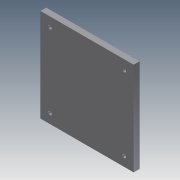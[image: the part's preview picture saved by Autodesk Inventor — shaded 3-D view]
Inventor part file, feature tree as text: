
AUTODESK INVENTOR PART (.ipt)
format: ipt  version: 2011 (Build 150239000, 239)  size: 496,640 bytes
history: native  units: in
note: dims shown in document units (in); Inventor stores cm internally (conversion verified against a paired STEP export)
features: extrude x49, sketch x49, fillet x2
ambient origin geometry x8: Origin, YZ Plane, XZ Plane, XY Plane, X Axis, Y Axis, Z Axis, Center Point
bodies: Solid1 (feature_tree)
feature tree (100):
  extrude  "Extrusion1"  Depth=4.0in
  extrude  "Extrusion2"  Depth=2.16in
  extrude  "Extrusion3"  Depth=1.7655in
  extrude  "Extrusion4"  Depth=0.029in TaperAngle=0.0deg
  extrude  "Extrusion5"  Depth=2.36in
  fillet  "Fillet1"  Radius=2.56in
  extrude  "Extrusion6"  Depth=0.125in
  extrude  "Extrusion7"  Depth=0.262in TaperAngle=0.0deg
  extrude  "Extrusion8"  Depth=0.029in TaperAngle=0.0deg
  extrude  "Extrusion9"  Depth=0.156in
  extrude  "Extrusion10"  Depth=0.5in TaperAngle=0.0deg
  extrude  "Extrusion11"  Depth=0.5in TaperAngle=0.0deg
  extrude  "Extrusion12"  Depth=1.875in TaperAngle=0.0deg
  extrude  "Extrusion13"  Depth=2.125in TaperAngle=0.0deg
  sketch  "Sketch14"  dims[d44=2.125in d45=0.0in d46=2.125in d47=0.0in]
  sketch  "Sketch15"  dims[d48=2.125in d49=0.0in d50=1.875in d51=0.0in]
  sketch  "Sketch16"  dims[d52=2.125in d53=0.0in d54=2.125in d55=0.0in]
  sketch  "Sketch17"  dims[d56=1.875in d57=0.0in d58=1.875in d59=0.0in]
  extrude  "Extrusion14"  Depth=2.125in TaperAngle=0.0deg
  extrude  "Extrusion15"  Depth=1.875in TaperAngle=0.0deg
  extrude  "Extrusion16"  Depth=2.125in TaperAngle=0.0deg
  extrude  "Extrusion17"  Depth=1.875in TaperAngle=0.0deg
  extrude  "Extrusion18"  Depth=2.125in TaperAngle=0.0deg
  extrude  "Extrusion19"  Depth=6.248in TaperAngle=0.0deg
  extrude  "Extrusion20"  Depth=1.281in
  extrude  "Extrusion21"  Depth=7.0in TaperAngle=0.0deg
  extrude  "Extrusion22"  Depth=2.0in
  extrude  "Extrusion23"  Depth=4.0in
  extrude  "Extrusion24"  Depth=2.0in
  extrude  "Extrusion25"  Depth=1.0in TaperAngle=0.0deg
  extrude  "Extrusion26"  Depth=0.25in
  extrude  "Extrusion27"  Depth=0.25in TaperAngle=0.0deg
  extrude  "Extrusion28"  Depth=0.25in TaperAngle=0.0deg
  extrude  "Extrusion29"  Depth=0.875in
  extrude  "Extrusion30"  Depth=0.5in TaperAngle=0.0deg
  extrude  "Extrusion31"  Depth=0.875in
  extrude  "Extrusion32"  Depth=0.5in TaperAngle=0.0deg
  extrude  "Extrusion33"  Depth=2.0in
  extrude  "Extrusion34"  Depth=4.0in
  fillet  "Fillet2"  Radius=1.0in
  extrude  "Extrusion35"  Depth=0.75in TaperAngle=0.0deg
  extrude  "Extrusion36"  Depth=0.9055in
  extrude  "Extrusion37"  Depth=0.8268in
  extrude  "Extrusion38"  Depth=0.75in TaperAngle=0.0deg
  extrude  "Extrusion39"  Depth=0.2559in
  extrude  "Extrusion40"  Depth=0.315in
  extrude  "Extrusion41"  Depth=1.063in
  extrude  "Extrusion42"  Depth=1.0in TaperAngle=0.0deg
  extrude  "Extrusion43"  Depth=0.406in
  extrude  "Extrusion44"  Depth=4.0in
  extrude  "Extrusion45"  [1 undecoded]
  extrude  "Extrusion46"  [1 undecoded]
  extrude  "Extrusion47"  [1 undecoded]
  extrude  "Extrusion48"  [1 undecoded]
  extrude  "Extrusion49"  [1 undecoded]
  sketch  "Sketch1"  dims[d0=4.0in d1=4.0in]
  sketch  "Sketch2"  dims[d2=0.029in d3=0.0in d4=2.16in]
  sketch  "Sketch3"  dims[d5=0.029in d6=0.0in d7=1.7655in]
  sketch  "Sketch4"  dims[d8=0.156in d9=0.029in d10=0.0in]
  sketch  "Sketch5"  dims[d11=0.029in d12=0.0in d13=2.36in d14=2.56in]
  sketch  "Sketch6"  dims[d15=0.262in d16=0.0in d17=0.125in]
  sketch  "Sketch7"  dims[d18=0.362in d19=0.0in d20=0.262in d21=0.0in]
  sketch  "Sketch8"  dims[d22=0.1in d23=0.0in d24=0.029in d25=0.0in]
  sketch  "Sketch9"  dims[d26=1.594in d27=0.156in]
  sketch  "Sketch10"  dims[d28=0.029in d29=0.0in d30=0.5in d31=0.0in]
  sketch  "Sketch11"  dims[d32=0.75in d33=0.0in d34=0.5in d35=0.0in]
  sketch  "Sketch12"  dims[d36=2.125in d37=0.0in d38=1.875in d39=0.0in]
  sketch  "Sketch13"  dims[d40=1.875in d41=0.0in d42=2.125in d43=0.0in]
  sketch  "Sketch18"  dims[d60=2.125in d61=0.0in d62=2.125in d63=0.0in]
  sketch  "Sketch19"  dims[d64=0.875in d65=0.0in d66=6.248in d67=0.0in]
  sketch  "Sketch20"  dims[d68=7.0in d69=0.0in d70=1.281in]
  sketch  "Sketch21"  dims[d71=3.188in d72=7.0in d73=0.0in]
  sketch  "Sketch22"  dims[d74=0.25in d75=0.0in d76=2.0in]
  sketch  "Sketch23"  dims[d77=2.0in d78=4.0in]
  sketch  "Sketch24"  dims[d79=1.0in d80=0.0in d81=2.0in]
  sketch  "Sketch25"  dims[d82=1.0in d83=1.0in d84=0.0in]
  sketch  "Sketch26"  dims[d85=0.5in d86=0.25in]
  sketch  "Sketch27"  dims[d87=0.25in d88=0.25in d89=0.0in]
  sketch  "Sketch28"  dims[d90=0.25in d91=0.0in d92=0.25in d93=0.0in]
  sketch  "Sketch29"  dims[d94=0.656in d95=0.875in]
  sketch  "Sketch30"  dims[d96=0.5in d97=0.0in d98=0.5in d99=0.0in]
  sketch  "Sketch31"  dims[d100=0.875in d101=0.875in]
  sketch  "Sketch32"  dims[d102=0.5in d103=0.0in d104=0.5in d105=0.0in]
  sketch  "Sketch33"  dims[d106=2.0in d107=2.0in]
  sketch  "Sketch34"  dims[d108=4.0in d109=4.0in d110=1.0in d111=0.0in]
  sketch  "Sketch35"  dims[d112=0.25in d113=0.0in d114=0.75in d115=0.0in]
  sketch  "Sketch36"  dims[d116=0.75in d117=0.0in d118=0.9055in]
  sketch  "Sketch37"  dims[d119=0.4134in d120=0.8268in]
  sketch  "Sketch38"  dims[d121=1.378in d122=0.75in d123=0.0in]
  sketch  "Sketch39"  dims[d124=0.5315in d125=0.2559in]
  sketch  "Sketch40"  dims[d126=0.315in d127=0.315in]
  sketch  "Sketch41"  dims[d128=1.063in d129=1.063in]
  sketch  "Sketch42"  dims[d130=0.0787in d131=1.0in d132=0.0in]
  sketch  "Sketch43"  dims[d133=0.25in d134=0.0in d135=0.406in]
  sketch  "Sketch44"  dims[d136=4.0in d137=4.0in]
  sketch  "Sketch45"  dims[d138=0.25in d139=0.0in]
  sketch  "Sketch46"
  sketch  "Sketch47"
  sketch  "Sketch48"
  sketch  "Sketch49"
note: 5 required parameter values undecoded (feature->parameter linkage not recoverable at this tier; creation-order binding heuristic only, values carry confidence <= 0.55)
